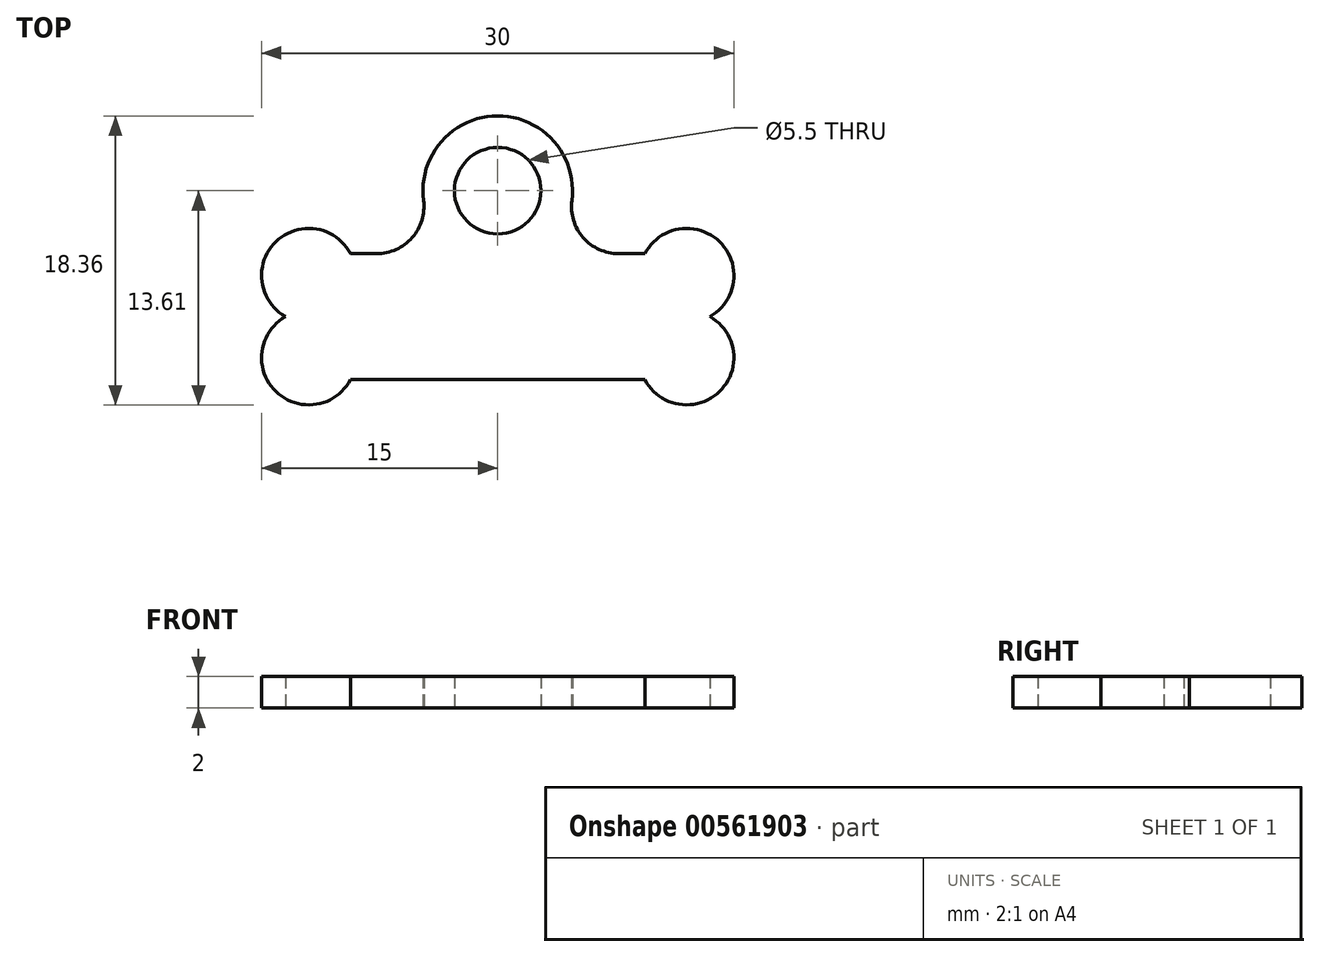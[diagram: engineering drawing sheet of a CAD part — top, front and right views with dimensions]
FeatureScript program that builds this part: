
annotation { "Feature Type Name" : "Feature", "Feature Type Description" : "" }
export const myFeature = defineFeature(function(context is Context, id is Id, definition is map)
    precondition{}
    {
        {
            var Q0;
            Q0=qCreatedBy(makeId("Top.planeOp"),FACE);
            var sketch = newSketch(context, id + "F0", { "sketchPlane" : qUnion([Q0]), "disableImprinting" : false});
            skLineSegment(sketch, "E0", {"start": v(-7.69, 4) * mm, "end": v(-9.34, 4) * mm});
            skArc(sketch, "E1", {"start": v(-9.34, 4) * mm, "mid": v(-14.08, 4.76) * mm, "end": v(-13.49, 0) * mm});
            skLineSegment(sketch, "E2", {"start": v(0, 0) * mm, "end": v(0, 4) * mm});
            skLineSegment(sketch, "E3", {"start": v(0, 0) * mm, "end": v(-13.49, 0) * mm});
            skLineSegment(sketch, "E4.MirrorCS", {"start": v(7.69, 4) * mm, "end": v(9.34, 4) * mm});
            skArc(sketch, "E5.MirrorCS", {"start": v(9.34, 4) * mm, "mid": v(14.08, 4.76) * mm, "end": v(13.49, 0) * mm});
            skArc(sketch, "E6.MirrorCS", {"start": v(-9.34, -4) * mm, "mid": v(-14.08, -4.76) * mm, "end": v(-13.49, 0) * mm});
            skLineSegment(sketch, "E7.MirrorCS", {"start": v(0, -4) * mm, "end": v(-9.34, -4) * mm});
            skLineSegment(sketch, "E8.MirrorCS", {"start": v(0, -4) * mm, "end": v(9.34, -4) * mm});
            skArc(sketch, "E9.MirrorCS", {"start": v(9.34, -4) * mm, "mid": v(14.08, -4.76) * mm, "end": v(13.49, 0) * mm});
            skCircle(sketch, "E10", {"center": v(0, 8) * mm, "radius": 2.75 * mm});
            skArc(sketch, "E11", {"start": v(4.71, 7.39) * mm, "mid": v(0, 12.75) * mm, "end": v(-4.71, 7.39) * mm});
            skPoint(sketch, "E12.orphan", {"position": v(0, 4) * mm});
            skPoint(sketch, "E13.visualSharp", {"position": v(2.56, 4) * mm});
            skArc(sketch, "E13.filletArc", {"start": v(4.71, 7.39) * mm, "mid": v(5.43, 5.02) * mm, "end": v(7.69, 4) * mm});
            skPoint(sketch, "E14.visualSharp", {"position": v(-2.56, 4) * mm});
            skArc(sketch, "E14.filletArc", {"start": v(-7.69, 4) * mm, "mid": v(-5.43, 5.02) * mm, "end": v(-4.71, 7.39) * mm});
            skSolve(sketch);
        }
        {
            var Q0;
            Q0=makeQuery(id+"F0.imprint","IMPRINT",FACE,{"disambiguationData":[TD([[makeQuery(id+"F0.imprint","IMPRINT",EDGE,{"derivedFrom":sQuery(id+"F0.wireOp",EDGE,"E0")}),1.0]])]});
            extrude(context, id + "F1", {"entities" : qUnion([Q0]), "depth" : 2 * mm, "offsetDistance" : 25 * mm});
        }
    });
